# Revit family: 2100.110 Rainhead Sump 360x360x280
name_source: partatom
category: Plumbing Fixtures
revit_build: Autodesk Revit 2016 (Build: 20150714_1515(x64)
units: mm (PartAtom-declared; Revit-internal decimal feet)

## family parameters
Always vertical = Yes
Cut with Voids When Loaded = No
OmniClass Number = 23.60.30.11
OmniClass Title = Pipework Products for General Use
Part Type = Normal
Room Calculation Point = No
Round Connector Dimension = Use Diameter
Shared = No
Work Plane-Based = No

## types (2) — shared parameters
CW Connection = No
Flow = 0.0 L/s
HW Connection = No
Manufacturer = Aquanight Industries Ltd
Material = Aquanight-Grey
Model = 2100.110
URL = www.aquaknight.co.nz
Vent Connection = No
Waste Connection = Yes

## per-type parameters (varying)
| type | Connector Diameter | Connector Location | Description |
| DWV100 | 100 mm  [stored 0.328084 ft] | 242 mm  [stored 0.793963 ft] | Rainhead 360x360x280 DWV100 DN100 |
| DWV150 | 150 mm | 176 mm  [stored 0.577428 ft] | Rainhead 360x360x280 DWV150 DN150 |

note: column(s) folded — value = type name in every type: Connector Description

note: [stored X ft] marks values corroborated as IEEE doubles in the binary element streams (Revit-internal decimal feet)

## geometry (parser evidence)
native form markers: Sweep x2
no freeform markers — native parametric forms only
